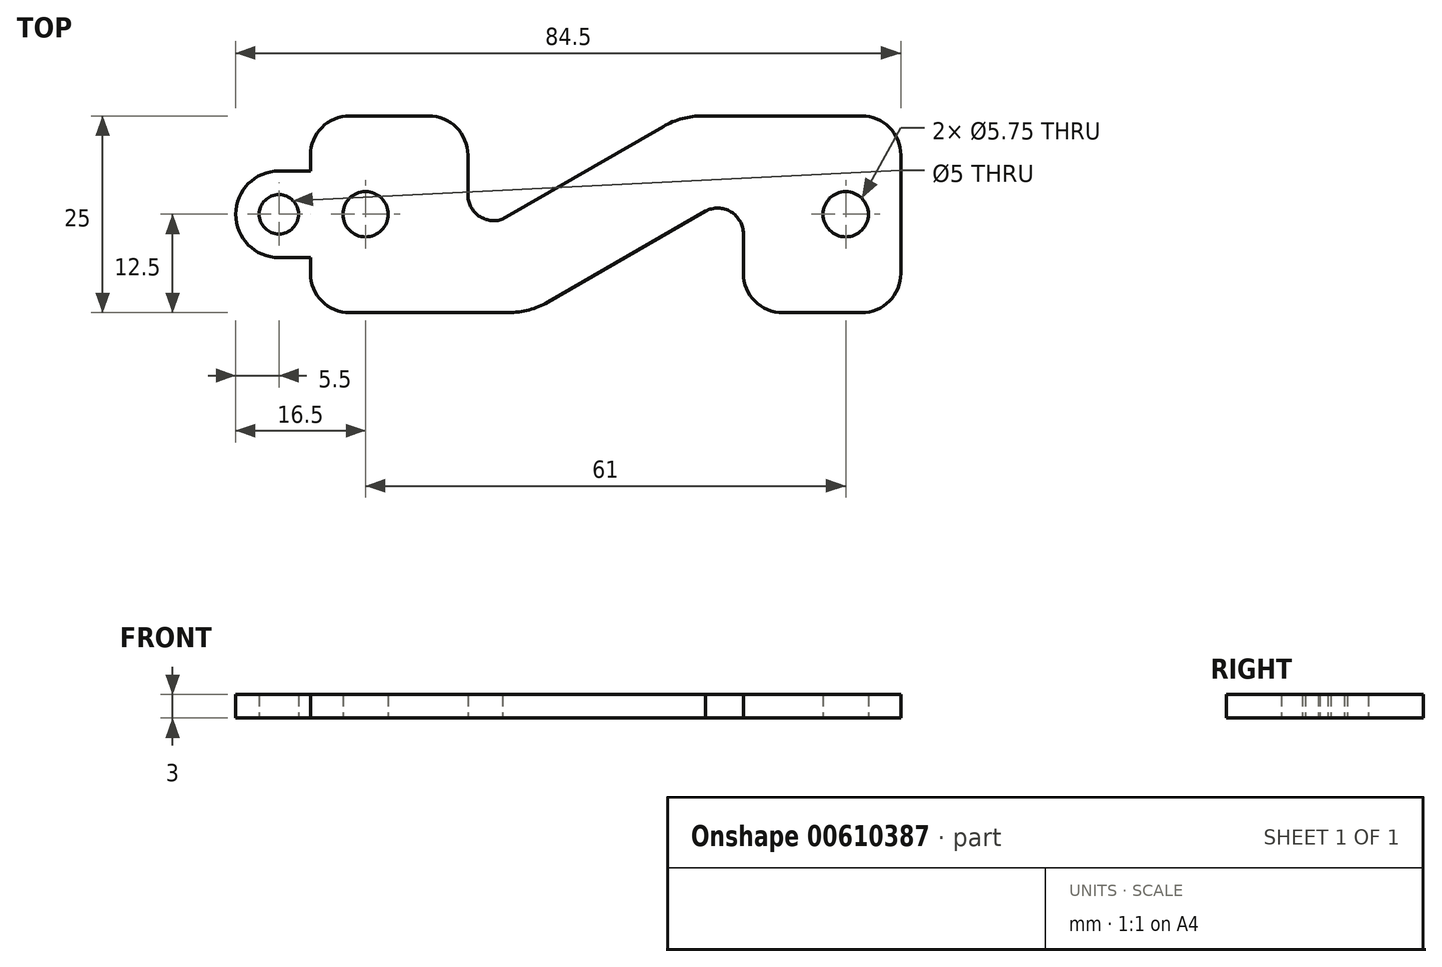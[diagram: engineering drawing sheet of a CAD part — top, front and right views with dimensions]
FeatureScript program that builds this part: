
annotation { "Feature Type Name" : "Feature", "Feature Type Description" : "" }
export const myFeature = defineFeature(function(context is Context, id is Id, definition is map)
    precondition{}
    {
        {
            var Q0;
            Q0=qCreatedBy(makeId("Top.planeOp"),FACE);
            var sketch = newSketch(context, id + "F0", { "sketchPlane" : qUnion([Q0])});
            skLineSegment(sketch, "E0.bottom", {"start": v(37.5, 12.5) * mm, "end": v(9.65, 12.5) * mm});
            skLineSegment(sketch, "E0.top", {"start": v(37.5, -12.5) * mm, "end": v(17.5, -12.5) * mm});
            skLineSegment(sketch, "E0.left", {"start": v(37.5, 12.5) * mm, "end": v(37.5, -12.5) * mm});
            skLineSegment(sketch, "E0.right", {"start": v(-37.5, 12.5) * mm, "end": v(-37.5, 5.5) * mm});
            skPoint(sketch, "E0.middle", {"position": v(0, 0) * mm});
            skLineSegment(sketch, "E1.0", {"start": v(-17.5, 12.5) * mm, "end": v(-17.5, 2.5) * mm});
            skLineSegment(sketch, "E2.0", {"start": v(17.5, -2.5) * mm, "end": v(17.5, -12.5) * mm});
            skLineSegment(sketch, "E3.trimOffspring", {"start": v(-9.65, -12.5) * mm, "end": v(-37.5, -12.5) * mm});
            skLineSegment(sketch, "E4.trimOffspring", {"start": v(-17.5, 12.5) * mm, "end": v(-37.5, 12.5) * mm});
            skCircle(sketch, "E5", {"center": v(-41.5, 0) * mm, "radius": 2.5 * mm});
            skArc(sketch, "E6.0", {"start": v(-41.5, 5.5) * mm, "mid": v(-47, 0) * mm, "end": v(-41.5, -5.5) * mm});
            skLineSegment(sketch, "E7", {"start": v(-41.5, 5.5) * mm, "end": v(-37.5, 5.5) * mm});
            skLineSegment(sketch, "E8", {"start": v(-41.5, -5.5) * mm, "end": v(-37.5, -5.5) * mm});
            skLineSegment(sketch, "E9.trimOffspring", {"start": v(-37.5, -5.5) * mm, "end": v(-37.5, -12.5) * mm});
            skLineSegment(sketch, "E10.0", {"start": v(-30.5, 12.5) * mm, "end": v(-30.5, -12.5) * mm, "construction": true});
            skCircle(sketch, "E11", {"center": v(-30.5, 0) * mm, "radius": 2.88 * mm});
            skCircle(sketch, "E12.MirrorC", {"center": v(30.5, 0) * mm, "radius": 2.88 * mm});
            skLineSegment(sketch, "E13", {"start": v(-10.44, -6.03) * mm, "end": v(10.48, 6.05) * mm});
            skLineSegment(sketch, "E14.0", {"start": v(-9.65, -12.5) * mm, "end": v(13.48, 0.85) * mm});
            skLineSegment(sketch, "E15.0", {"start": v(-13.44, -0.83) * mm, "end": v(9.65, 12.5) * mm});
            skArc(sketch, "E16", {"start": v(-17.5, 2.5) * mm, "mid": v(-15.55, -0.52) * mm, "end": v(-12, 0) * mm});
            skArc(sketch, "E17", {"start": v(17.5, -2.5) * mm, "mid": v(15.9, 0.31) * mm, "end": v(12.68, 0.4) * mm});
            skSolve(sketch);
        }
        {
            var Q0;
            Q0 = qSketchRegion(id + "F0", true);
            extrude(context, id + "F1", {"entities" : qUnion([Q0]), "depth" : 3 * mm, "offsetDistance" : 25 * mm});
        }
        {
            var Q0;
            Q0=makeQuery(id+"F1.opExtrude","SWEPT_EDGE",EDGE,{"disambiguationData":[OSD([sQuery(id+"F0.wireOp",EDGE,"E1.0"),sQuery(id+"F0.wireOp",EDGE,"E4.trimOffspring")])]});
            var Q1;
            Q1=makeQuery(id+"F1.opExtrude","SWEPT_EDGE",EDGE,{"disambiguationData":[OSD([sQuery(id+"F0.wireOp",EDGE,"E0.top"),sQuery(id+"F0.wireOp",EDGE,"E2.0")])]});
            var Q2;
            Q2=makeQuery(id+"F1.opExtrude","SWEPT_EDGE",EDGE,{"disambiguationData":[OSD([sQuery(id+"F0.wireOp",EDGE,"E0.top"),sQuery(id+"F0.wireOp",EDGE,"E0.left")])]});
            var Q3;
            Q3=makeQuery(id+"F1.opExtrude","SWEPT_EDGE",EDGE,{"disambiguationData":[OSD([sQuery(id+"F0.wireOp",EDGE,"E0.bottom"),sQuery(id+"F0.wireOp",EDGE,"E0.left")])]});
            var Q4;
            Q4=makeQuery(id+"F1.opExtrude","SWEPT_EDGE",EDGE,{"disambiguationData":[OSD([sQuery(id+"F0.wireOp",EDGE,"E3.trimOffspring"),sQuery(id+"F0.wireOp",EDGE,"E9.trimOffspring")])]});
            var Q5;
            Q5=makeQuery(id+"F1.opExtrude","SWEPT_EDGE",EDGE,{"disambiguationData":[OSD([sQuery(id+"F0.wireOp",EDGE,"E0.right"),sQuery(id+"F0.wireOp",EDGE,"E4.trimOffspring")])]});
            fillet(context, id + "F2", {"entities" : qUnion([Q0, Q1, Q2, Q3, Q4, Q5]), "radius" : 5 * mm, "tangentPropagation" : true, "allowEdgeOverflow" : false});
        }
        {
            var Q0;
            Q0=makeQuery(id+"F1.opExtrude","SWEPT_EDGE",EDGE,{"disambiguationData":[OSD([sQuery(id+"F0.wireOp",EDGE,"E3.trimOffspring"),sQuery(id+"F0.wireOp",EDGE,"E14.0")])]});
            var Q1;
            Q1=makeQuery(id+"F1.opExtrude","SWEPT_EDGE",EDGE,{"disambiguationData":[OSD([sQuery(id+"F0.wireOp",EDGE,"E0.bottom"),sQuery(id+"F0.wireOp",EDGE,"E15.0")])]});
            fillet(context, id + "F3", {"entities" : qUnion([Q0, Q1]), "radius" : 10 * mm, "tangentPropagation" : true, "allowEdgeOverflow" : false});
        }
    });
